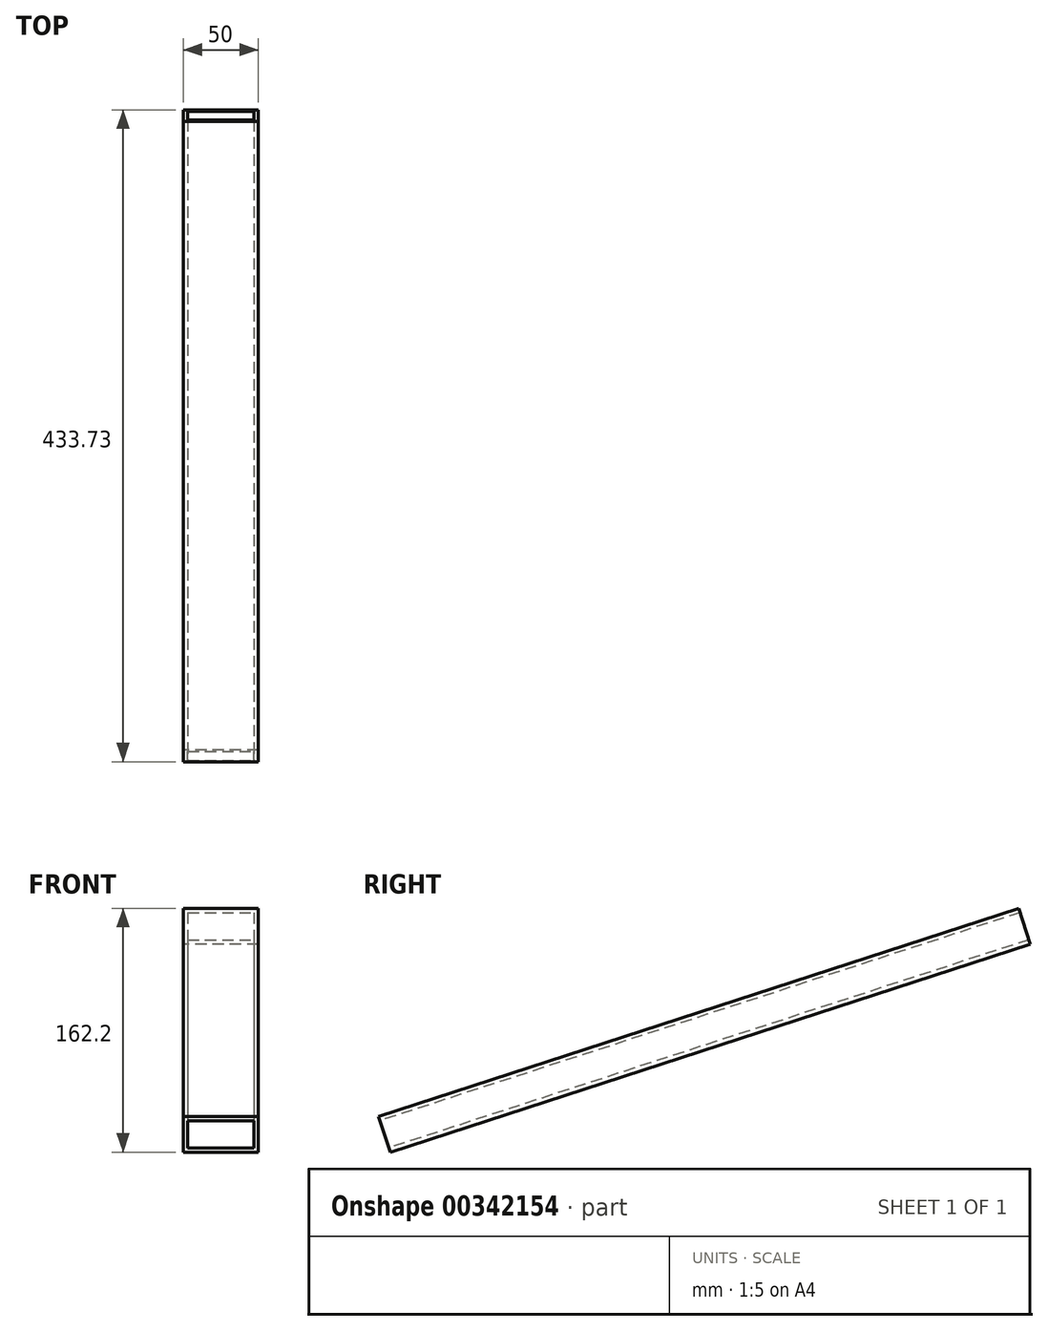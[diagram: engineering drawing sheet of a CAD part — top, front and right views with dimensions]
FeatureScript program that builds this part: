
annotation { "Feature Type Name" : "Feature", "Feature Type Description" : "" }
export const myFeature = defineFeature(function(context is Context, id is Id, definition is map)
    precondition{}
    {
        {
            var Q0;
            Q0=qCreatedBy(makeId("Right.planeOp"),FACE);
            var sketch = newSketch(context, id + "F0", { "sketchPlane" : qUnion([Q0])});
            skLineSegment(sketch, "E0", {"start": v(0, 0) * mm, "end": v(2288, 0) * mm});
            skLineSegment(sketch, "E1", {"start": v(2288, 0) * mm, "end": v(2288, 684.37) * mm});
            skLineSegment(sketch, "E2", {"start": v(2100, 0) * mm, "end": v(2100, 623.29) * mm});
            skLineSegment(sketch, "E3", {"start": v(2050, 0) * mm, "end": v(2050, 607.04) * mm});
            skLineSegment(sketch, "E4", {"start": v(2100, 623.29) * mm, "end": v(2288, 684.37) * mm});
            skLineSegment(sketch, "E5", {"start": v(2100, 623.29) * mm, "end": v(2050, 607.04) * mm});
            skLineSegment(sketch, "E6", {"start": v(2050, 607.04) * mm, "end": v(1862, 545.95) * mm});
            skLineSegment(sketch, "E7", {"start": v(2100, 623.29) * mm, "end": v(2092.27, 647.06) * mm});
            skLineSegment(sketch, "E8", {"start": v(2050, 607.04) * mm, "end": v(2042.27, 630.82) * mm});
            skLineSegment(sketch, "E9", {"start": v(2288, 684.37) * mm, "end": v(2280.27, 708.15) * mm});
            skLineSegment(sketch, "E10", {"start": v(2280.27, 708.15) * mm, "end": v(2092.27, 647.06) * mm});
            skLineSegment(sketch, "E11", {"start": v(2092.27, 647.06) * mm, "end": v(2042.27, 630.82) * mm});
            skLineSegment(sketch, "E12", {"start": v(2042.27, 630.82) * mm, "end": v(1854.27, 569.73) * mm});
            skLineSegment(sketch, "E13", {"start": v(1854.27, 569.73) * mm, "end": v(1862, 545.95) * mm});
            skLineSegment(sketch, "E14", {"start": v(1853.35, 572.58) * mm, "end": v(2279.35, 711) * mm});
            skLineSegment(sketch, "E15", {"start": v(2280.27, 708.15) * mm, "end": v(2279.35, 711) * mm});
            skLineSegment(sketch, "E16", {"start": v(1854.27, 569.73) * mm, "end": v(1853.35, 572.58) * mm});
            skSolve(sketch);
        }
        {
            var Q0;
            {var subQ0=sQuery(id+"F0.wireOp",EDGE,"ijd3VTFd-Imta-bpwi-KAd7-0lDIgMz6j6Lr");var subQ1=sQuery(id+"F0.wireOp",EDGE,"E3");var subQ2=makeQuery(id+"F0.imprint","INTERSECT",VERTEX,{"derivedFrom":[subQ1,subQ0]});Q0=makeQuery(id+"F0.imprint","IMPRINT",FACE,{"disambiguationData":[TD([[makeQuery(id+"F0.imprint","IMPRINT",EDGE,{"disambiguationData":[TD([[subQ2,1.0]])],"derivedFrom":subQ1}),1.0]])]});}
            var Q1;
            Q1=makeQuery(id+"F0.imprint","IMPRINT",FACE,{"disambiguationData":[TD([[makeQuery(id+"F0.imprint","IMPRINT",EDGE,{"derivedFrom":sQuery(id+"F0.wireOp",EDGE,"E6")}),-1.0]])]});
            var Q2;
            Q2=makeQuery(id+"F0.imprint","IMPRINT",FACE,{"disambiguationData":[TD([[makeQuery(id+"F0.imprint","IMPRINT",EDGE,{"derivedFrom":sQuery(id+"F0.wireOp",EDGE,"E5")}),-1.0]])]});
            var Q3;
            Q3=makeQuery(id+"F0.imprint","IMPRINT",FACE,{"disambiguationData":[TD([[makeQuery(id+"F0.imprint","IMPRINT",EDGE,{"derivedFrom":sQuery(id+"F0.wireOp",EDGE,"E4")}),1.0]])]});
            extrude(context, id + "F1", {"entities" : qUnion([Q0, Q1, Q2, Q3]), "endBound" : BoundingType.SYMMETRIC, "depth" : 50 * mm});
        }
        {
            var Q0;
            Q0=makeQuery(id+"F1.opExtrude","SWEPT_FACE",FACE,{"disambiguationData":[OSD([sQuery(id+"F0.wireOp",EDGE,"E13")])]});
            var sketch = newSketch(context, id + "F2", { "sketchPlane" : qUnion([Q0])});
            skLineSegment(sketch, "E17.bottom", {"start": v(-22, -34.16) * mm, "end": v(22, -34.16) * mm});
            skLineSegment(sketch, "E17.top", {"start": v(-22, -53.16) * mm, "end": v(22, -53.16) * mm});
            skLineSegment(sketch, "E17.left", {"start": v(-22, -34.16) * mm, "end": v(-22, -53.16) * mm});
            skLineSegment(sketch, "E17.right", {"start": v(22, -34.16) * mm, "end": v(22, -53.16) * mm});
            skPoint(sketch, "E17.middle", {"position": v(0, -43.66) * mm});
            skPoint(sketch, "E17.middle.positionSnap0", {"position": v(0, -31.16) * mm});
            skPoint(sketch, "E17.middle.positionSnap1", {"position": v(25, -43.66) * mm});
            skPoint(sketch, "E17.centerSnap1", {"position": v(25, -43.66) * mm});
            skSolve(sketch);
        }
        {
            var Q0;
            Q0=qSketchRegion(id+"F2",true);
            extrude(context, id + "F3", {"entities" : qUnion([Q0]), "operationType" : NewBodyOperationType.REMOVE, "endBound" : BoundingType.THROUGH_ALL, "oppositeDirection" : true, "depth" : 300 * mm});
        }
    });
